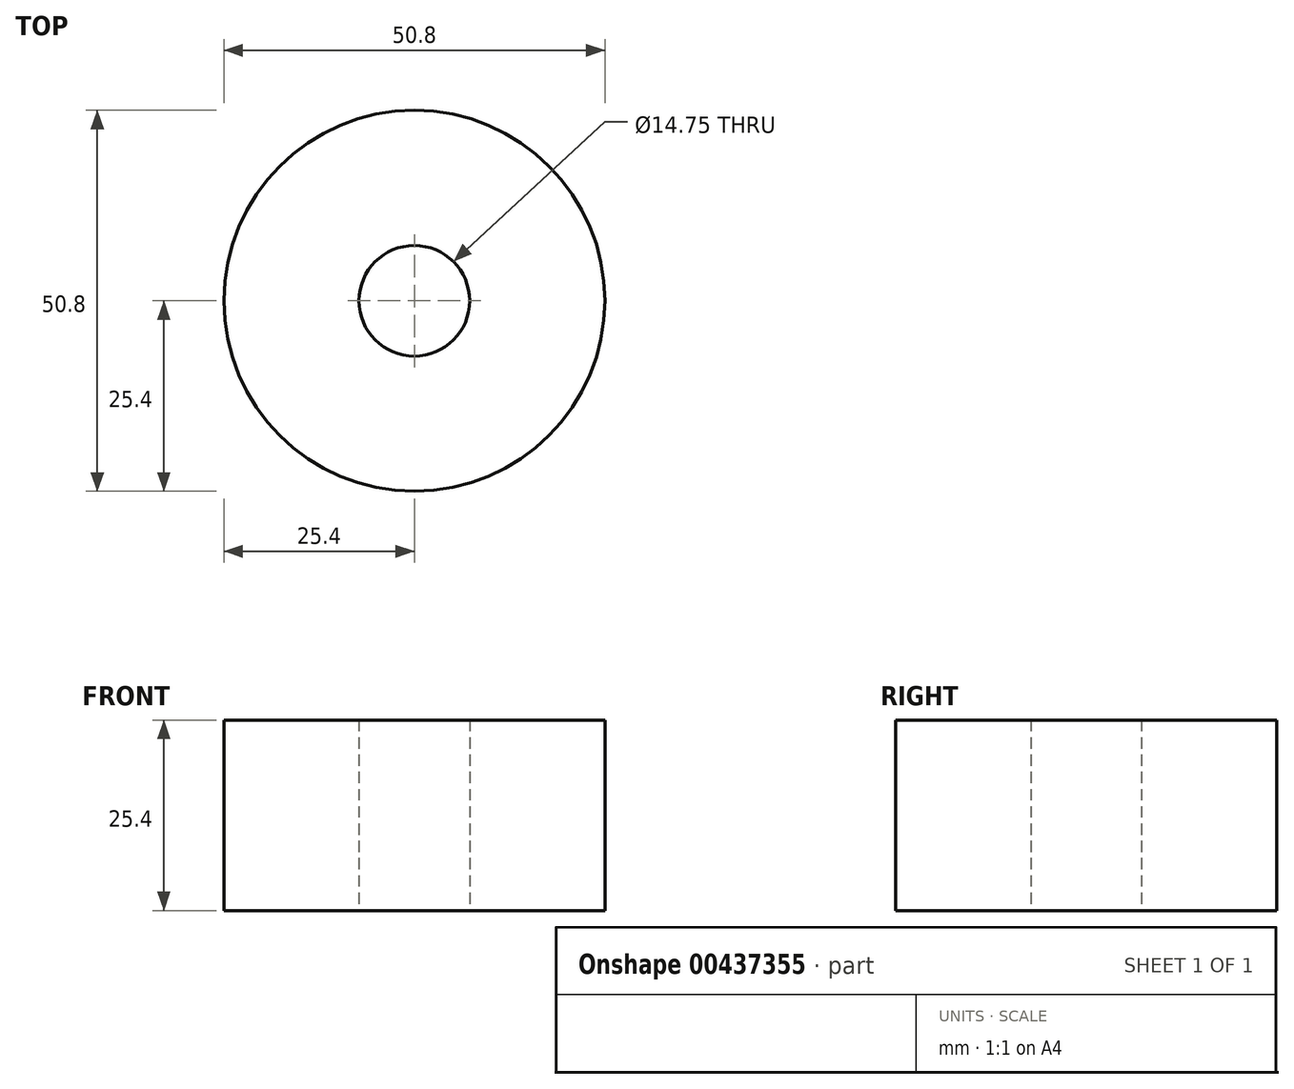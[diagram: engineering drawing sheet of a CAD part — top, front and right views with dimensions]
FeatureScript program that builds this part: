
annotation { "Feature Type Name" : "Feature", "Feature Type Description" : "" }
export const myFeature = defineFeature(function(context is Context, id is Id, definition is map)
    precondition{}
    {
        {
            var Q0;
            Q0=qCreatedBy(makeId("Top.planeOp"),FACE);
            var sketch = newSketch(context, id + "F0", { "sketchPlane" : qUnion([Q0])});
            skCircle(sketch, "E0", {"center": v(0, 0) * mm, "radius": 25.4 * mm});
            skCircle(sketch, "E1", {"center": v(0, 0) * mm, "radius": 7.37 * mm});
            skSolve(sketch);
        }
        {
            var Q0;
            Q0 = qSketchRegion(id + "F0", true);
            extrude(context, id + "F1", {"entities" : qUnion([Q0]), "depth" : 25.4 * mm});
        }
    });
